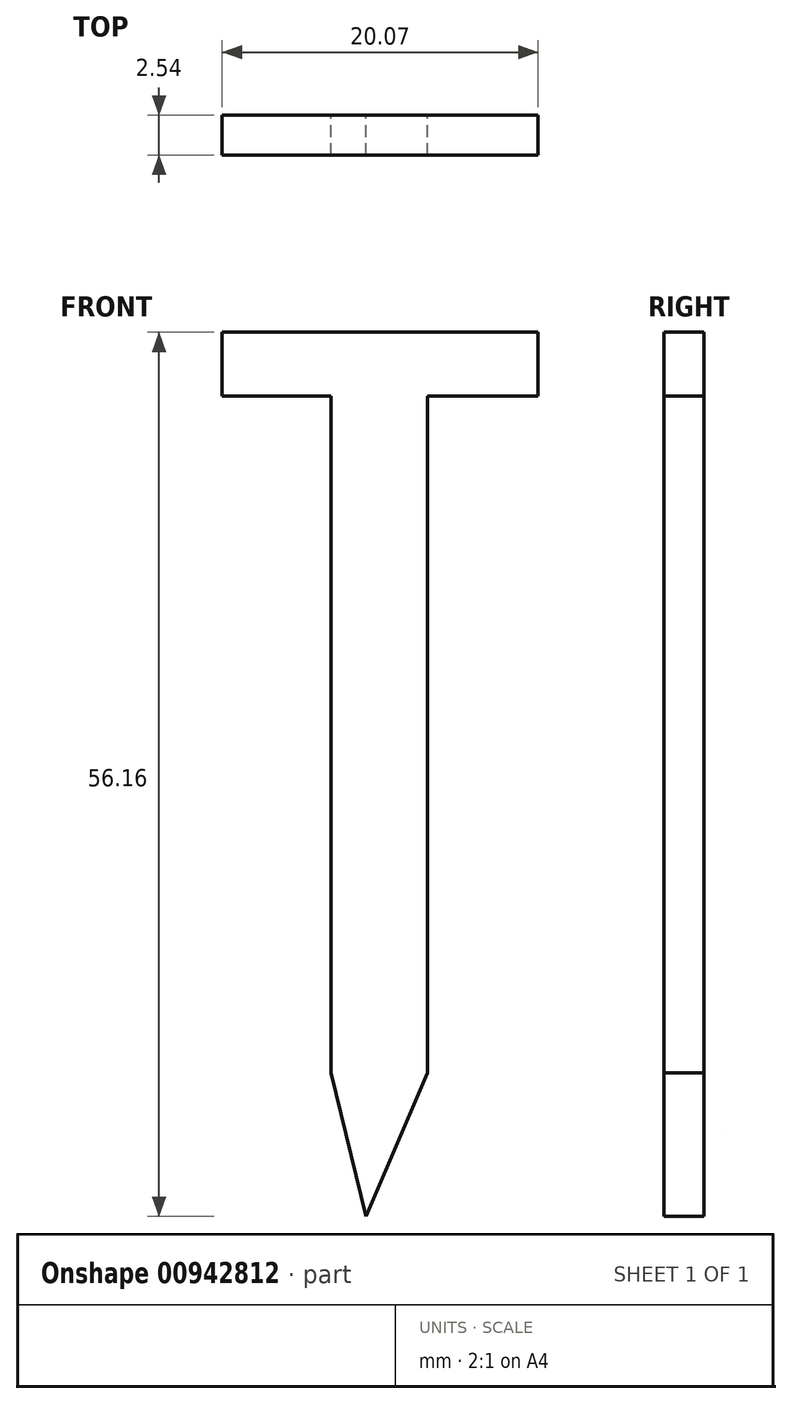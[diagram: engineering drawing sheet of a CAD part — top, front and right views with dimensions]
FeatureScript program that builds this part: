
annotation { "Feature Type Name" : "Feature", "Feature Type Description" : "" }
export const myFeature = defineFeature(function(context is Context, id is Id, definition is map)
    precondition{}
    {
        {
            var Q0;
            Q0=qCreatedBy(makeId("Front.planeOp"),FACE);
            var sketch = newSketch(context, id + "F0", { "sketchPlane" : qUnion([Q0])});
            skLineSegment(sketch, "E0", {"start": v(-61.05, -15.83) * mm, "end": v(-58.83, -24.95) * mm});
            skLineSegment(sketch, "E1", {"start": v(-58.83, -24.95) * mm, "end": v(-54.93, -15.83) * mm});
            skLineSegment(sketch, "E2", {"start": v(-54.93, -15.83) * mm, "end": v(-54.93, 27.17) * mm});
            skLineSegment(sketch, "E3", {"start": v(-61.05, -15.83) * mm, "end": v(-61.05, 27.17) * mm});
            skLineSegment(sketch, "E4", {"start": v(-61.05, 27.17) * mm, "end": v(-67.96, 27.17) * mm});
            skLineSegment(sketch, "E5", {"start": v(-67.96, 27.17) * mm, "end": v(-67.96, 31.2) * mm});
            skLineSegment(sketch, "E6", {"start": v(-67.96, 31.2) * mm, "end": v(-47.89, 31.2) * mm});
            skLineSegment(sketch, "E7", {"start": v(-47.89, 31.2) * mm, "end": v(-47.89, 27.17) * mm});
            skLineSegment(sketch, "E8", {"start": v(-47.89, 27.17) * mm, "end": v(-54.93, 27.17) * mm});
            skSolve(sketch);
        }
        {
            var Q0;
            Q0 = qSketchRegion(id + "F0", true);
            extrude(context, id + "F1", {"entities" : qUnion([Q0]), "depth" : 2.54 * mm, "offsetDistance" : 25.4 * mm});
        }
    });
